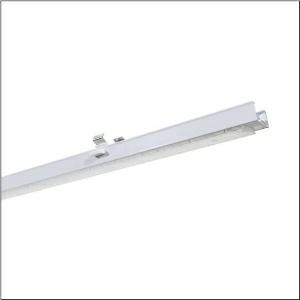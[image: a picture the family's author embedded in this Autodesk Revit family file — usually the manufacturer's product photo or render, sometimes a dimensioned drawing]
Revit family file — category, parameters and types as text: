
# Revit family: trunking_flex_31_51re12mb68b
name_source: partatom
category: Lighting Fixtures
units: mm (PartAtom-declared; Revit-internal decimal feet)

## family parameters
Cut with Voids When Loaded = No
Host = Face
Light Source = No
Part Type = Normal
Room Calculation Point = No
Round Connector Dimension = Use Diameter
Shared = No

## types (1)
- --- (1 x LED, 8000 lm, 50 W, 6500K)
    Apparent Load = 50 VA
    CIE Flux Codes = 65 91 98 99 100
    Color Rendering = 80
    Color Temperature = 6500K
    Default Elevation = 1800 mm
    Description = Trunking Flex 31, luminaire insert, of extruded aluminium section, coated, traffic white (RAL 9016), length: 1.472mm, width: 91mm, height: 53mm, LED rated luminous flux: 8.000lm, light colour: 865, SDCM (Standard Deviation of Colour Matching)MacAdam ≤ 3 SDCM (initial), control gear: ON/OFF Multilumen, with system connector: socket, mains connection: 220..240V, AC, 50/60Hz, rated input power: 50W, luminous flux adjustable on luminaire in four steps (4130/5610/6850/8000lm), connected load according to luminous flux setting (25/34/42/50W), primary light control with lens, of plastic, primary optical cover: cover, of PMMA, light emission: direct distribution, protection rating (complete): IP20, insulation class (complete): insulation class I (protective earthing), certification: CE, UKCA, impact resistance: IK02, permissible ambient temperature for indoor applications: -20..+40°C, packaging unit: 1 piece
    Height = 58 mm
    Lamp = 1 x LED
    Lamp Light Flux = 8000 lm
    Lamp Power = 50 W
    Lamp count = 1
    Length = 1472 mm
    Luminous efficacy = 160 lm/W
    Manufacturer = Siteco
    ModVariant = No
    Model = 51RE12MB68B
    Mounting Place = Ceiling
    Mounting Type = Pendant
    Number of Poles = 1
    OnlyDefault = Yes
    Power Factor = 1
    Product Name = Trunking Flex 31
    Product group = luminaire insert | ceiling pendant
    ProductGroupID = 901
    Protection Class = Protection class I
    Protection Degree = IP 20
    RLX_Detail_Level = 1
    RLX_Emergency_Light_Flux = 0 lm
    RLX_Emergency_Type = 0
    RLX_Emergency_Type_DB = No
    RlxData = <blob elided: 20385 chars, md5=703983f7>
    Socket = socket
    Standby Power = 0 W
    System Light Flux = 8000 lm
    System Power = 50 W
    Type Comments = factory setting: luminous flux: 100 % | (ON | ON) | 300 mA
    Type Image = l_1266702.jpg
    URL = http://relux.com
    VarID = @adj_065521
    Voltage = 0 V
    Weight = 0.00 kg
    Width = 65 mm

## geometry (parser evidence)
native form markers: Blend x4, Sweep x9
no freeform markers — native parametric forms only
